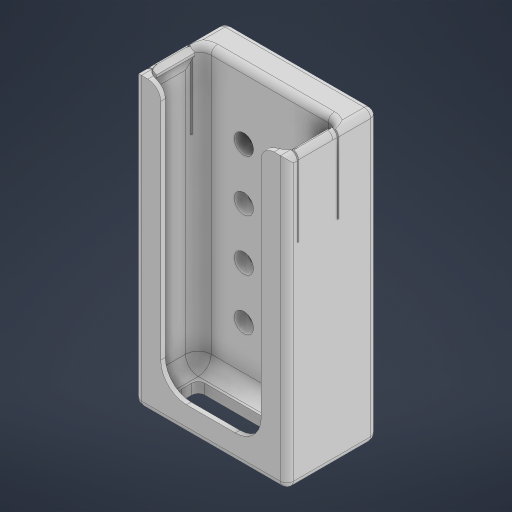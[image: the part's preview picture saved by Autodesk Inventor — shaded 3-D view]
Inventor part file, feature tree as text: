
AUTODESK INVENTOR PART (.ipt)
format: ipt  version: 2023 (Build 270158000, 158)  size: 408,064 bytes
history: native  units: in
note: dims shown in document units (in); Inventor stores cm internally (conversion verified against a paired STEP export)
features: sketch x7, extrude x6, fillet x4, projected_geometry x2, mirror x1, hole x1, pattern_linear x1
ambient origin geometry x8: Origin, YZ Plane, XZ Plane, XY Plane, X Axis, Y Axis, Z Axis, Center Point
bodies: Solid1 (feature_tree)
feature tree (22):
  extrude  "Extrusion1"  Depth=5.4in
  extrude  "Extrusion2"  Depth=1.75in TaperAngle=0.0deg
  extrude  "Extrusion3"  Depth=0.09in
  fillet  "Fillet1"  Radius=0.09in
  extrude  "Extrusion4"  Depth=5.4in TaperAngle=0.0deg
  extrude  "Extrusion5"  Depth=0.5in
  mirror  "Mirror1"
  extrude  "Extrusion6"  Depth=5.25in TaperAngle=0.0deg
  hole  "Hole1"  [1 undecoded]
  pattern_linear  "Rectangular Pattern1"  Spacing1=0.025in  [1 undecoded]
  fillet  "Fillet2"  Radius=0.025in
  fillet  "Fillet3"  Radius=0.75in
  fillet  "Fillet4"  Radius=1.5in
  sketch  "Sketch1"  dims[d0=2.75in d1=5.4in]
  sketch  "Sketch2"  dims[d2=0.1in d3=1.75in d4=0.0in]
  sketch  "Sketch3"  dims[d5=0.09in d6=0.09in d7=0.09in]
  sketch  "Sketch4"  dims[d8=1.05in d9=5.4in d10=0.0in]
  sketch  "Sketch5"  dims[d11=0.5in d12=0.5in]
  projected_geometry  "Projected Loop1"
  sketch  "Sketch6"  dims[d13=0.5in d14=5.25in d15=0.0in]
  projected_geometry  "Projected Loop2"
  sketch  "Sketch7"  dims[d16=0.25in d17=0.2in d18=0.025in d19=0.025in d20=0.75in d21=1.5in d22=0.0in d23=0.0in d30=1.0in d31=0.0in d32=0.1in d33=0.05in d34=0.375in d35=0.375in d36=0.375in d37=0.075in d38=0.05in d39=1.0in d40=0.0in d42=0.5in d43=1.5in d44=0.156in d45=0.38in d46=0.375in d47=0.25in d48=0.5635in d49=1.0in d50=0.8108in d51=0.7874in d53=1.0in d54=1.5748in d56=1.0in d57=0.5in d58=0.25in d59=0.125in]
note: 2 required parameter values undecoded (feature->parameter linkage not recoverable at this tier; creation-order binding heuristic only, values carry confidence <= 0.55)
